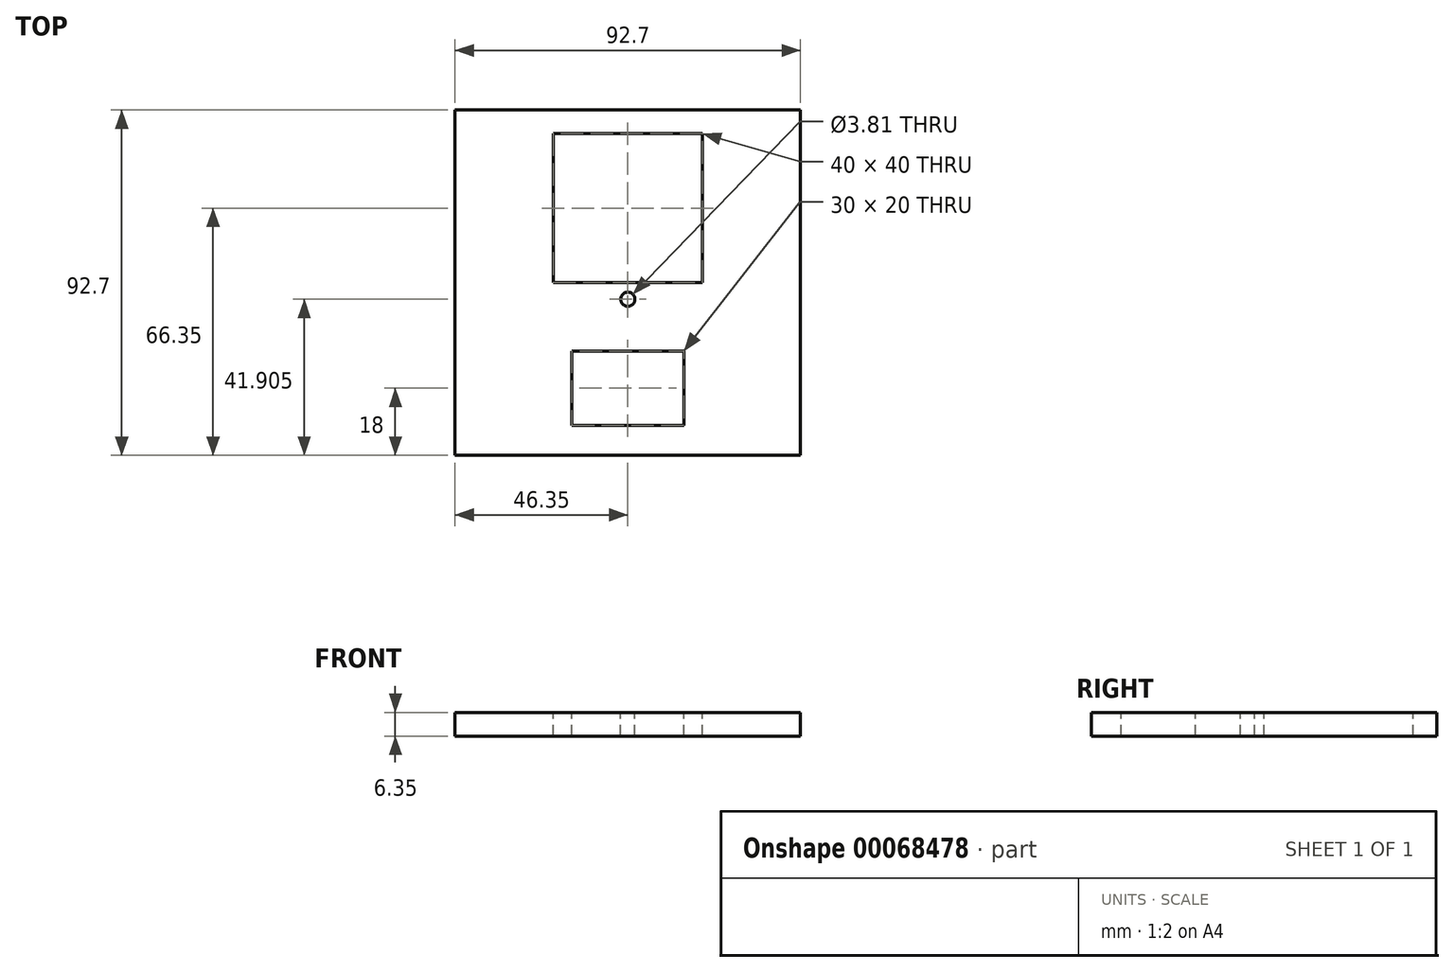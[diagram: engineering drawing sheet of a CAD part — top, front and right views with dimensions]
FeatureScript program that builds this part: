
annotation { "Feature Type Name" : "Feature", "Feature Type Description" : "" }
export const myFeature = defineFeature(function(context is Context, id is Id, definition is map)
    precondition{}
    {
        {
            var Q0;
            Q0=qCreatedBy(makeId("Top.planeOp"),FACE);
            var sketch = newSketch(context, id + "F0", { "sketchPlane" : qUnion([Q0])});
            skLineSegment(sketch, "E0.rect.bottom", {"start": v(46.35, -46.35) * mm, "end": v(-46.35, -46.35) * mm});
            skLineSegment(sketch, "E0.rect.top", {"start": v(46.35, 46.35) * mm, "end": v(-46.35, 46.35) * mm});
            skLineSegment(sketch, "E0.rect.left", {"start": v(46.35, -46.35) * mm, "end": v(46.35, 46.35) * mm});
            skLineSegment(sketch, "E0.rect.right", {"start": v(-46.35, -46.35) * mm, "end": v(-46.35, 46.35) * mm});
            skPoint(sketch, "E0.rect.middle", {"position": v(0, 0) * mm});
            skSolve(sketch);
        }
        {
            var Q0;
            Q0 = qSketchRegion(id + "F0", true);
            extrude(context, id + "F1", {"entities" : qUnion([Q0]), "depth" : 6.35 * mm});
        }
        {
            var Q0;
            Q0=makeQuery(id+"F1.opExtrude","CAP_FACE",FACE,{"disambiguationData":[OSD([sQuery(id+"F0.wireOp",EDGE,"E0.rect.bottom"),sQuery(id+"F0.wireOp",EDGE,"E0.rect.top"),sQuery(id+"F0.wireOp",EDGE,"E0.rect.left"),sQuery(id+"F0.wireOp",EDGE,"E0.rect.right")])],"isStart":false});
            var sketch = newSketch(context, id + "F2", { "sketchPlane" : qUnion([Q0])});
            skLineSegment(sketch, "E1.bottom", {"start": v(20, 40) * mm, "end": v(-20, 40) * mm});
            skLineSegment(sketch, "E1.top", {"start": v(20, 0) * mm, "end": v(-20, 0) * mm});
            skLineSegment(sketch, "E1.left", {"start": v(20, 40) * mm, "end": v(20, 0) * mm});
            skLineSegment(sketch, "E1.right", {"start": v(-20, 40) * mm, "end": v(-20, 0) * mm});
            skLineSegment(sketch, "E2", {"start": v(20, 40) * mm, "end": v(20, 46.35) * mm, "construction": true});
            skLineSegment(sketch, "E3", {"start": v(20, 40) * mm, "end": v(46.35, 40) * mm, "construction": true});
            skLineSegment(sketch, "E4.bottom", {"start": v(-15, -38.35) * mm, "end": v(15, -38.35) * mm});
            skLineSegment(sketch, "E4.top", {"start": v(-15, -18.35) * mm, "end": v(15, -18.35) * mm});
            skLineSegment(sketch, "E4.left", {"start": v(-15, -38.35) * mm, "end": v(-15, -18.35) * mm});
            skLineSegment(sketch, "E4.right", {"start": v(15, -38.35) * mm, "end": v(15, -18.35) * mm});
            skLineSegment(sketch, "E5", {"start": v(-15, -38.35) * mm, "end": v(-46.35, -38.35) * mm, "construction": true});
            skLineSegment(sketch, "E6", {"start": v(-15, -38.35) * mm, "end": v(-15, -46.35) * mm, "construction": true});
            skCircle(sketch, "E7", {"center": v(0, -4.45) * mm, "radius": 1.9 * mm});
            skLineSegment(sketch, "E8", {"start": v(0, -6.35) * mm, "end": v(0, -46.35) * mm, "construction": true});
            skPoint(sketch, "E9.start.orphan", {"position": v(0, -2.54) * mm});
            skSolve(sketch);
        }
        {
            var Q0;
            Q0=makeQuery(id+"F2.imprint","IMPRINT",FACE,{"disambiguationData":[TD([[makeQuery(id+"F2.imprint","IMPRINT",EDGE,{"derivedFrom":sQuery(id+"F2.wireOp",EDGE,"E4.bottom")}),1.0]])]});
            var Q1;
            Q1=makeQuery(id+"F2.imprint","IMPRINT",FACE,{"disambiguationData":[TD([[makeQuery(id+"F2.imprint","IMPRINT",EDGE,{"derivedFrom":sQuery(id+"F2.wireOp",EDGE,"E1.bottom")}),1.0]])]});
            var Q2;
            Q2=makeQuery(id+"F2.imprint","IMPRINT",FACE,{"disambiguationData":[TD([[makeQuery(id+"F2.imprint","IMPRINT",EDGE,{"derivedFrom":sQuery(id+"F2.wireOp",EDGE,"E7")}),1.0]])]});
            extrude(context, id + "F3", {"entities" : qUnion([Q0, Q1, Q2]), "operationType" : NewBodyOperationType.REMOVE, "endBound" : BoundingType.THROUGH_ALL, "oppositeDirection" : true, "depth" : 6.35 * mm});
        }
    });
